# Revit family: AAC23
name_source: partatom
category: Furniture
revit_build: Autodesk Revit 2016 (Build: 20161004_0715(x64)
units: mm (PartAtom-declared; Revit-internal decimal feet)

## family parameters
Always vertical = Yes
Cut with Voids When Loaded = No
OmniClass Number = 23.40.20.00
OmniClass Title = General Furniture and Specialties
Room Calculation Point = No
Shared = No
Work Plane-Based = No

## types (1)
- AAC23
    Base = HAY Matt laquered Oak Horizontal
    Depth = 52cm - 20.47inch
    Description = A classic and versatile chair featuring an upholstered solid shell and armrests and wooden base. Equally suitable for homes, offices and public spaces.
    Design = Hee Welling & HAY
    Gliders = HAY Black Standard Glider
    Height = 79cm - 31.10inch
    Manufacturer = HAY
    Model = AAC 23 Moulded plywood legs
    Optional Upholstery = Full upholstery
    Price = Contact HAY or visit hay.dk
    Seat Height = 46cm - 18.11inch
    Shell = HAY Hallingdal - 130
    Strength, durability and safety = EN 16139:2013 L2
    Type Comments = Injection moulded polypropylene shell with full upholstery.
    URL = http://hay.dk
    Upholstery fabric = Available in a large selection of standard fabrics and leathers.
    Variations = Variability of textiles, colours and base finishes.  Other base options are: 4-leg steel base, sled base, swivel base, wheel base and solid wood legs. Shell is also available without armrest.
    Width = 59cm - 23.23inch

## geometry (parser evidence)
native form markers: Sweep x2
no freeform markers — native parametric forms only
